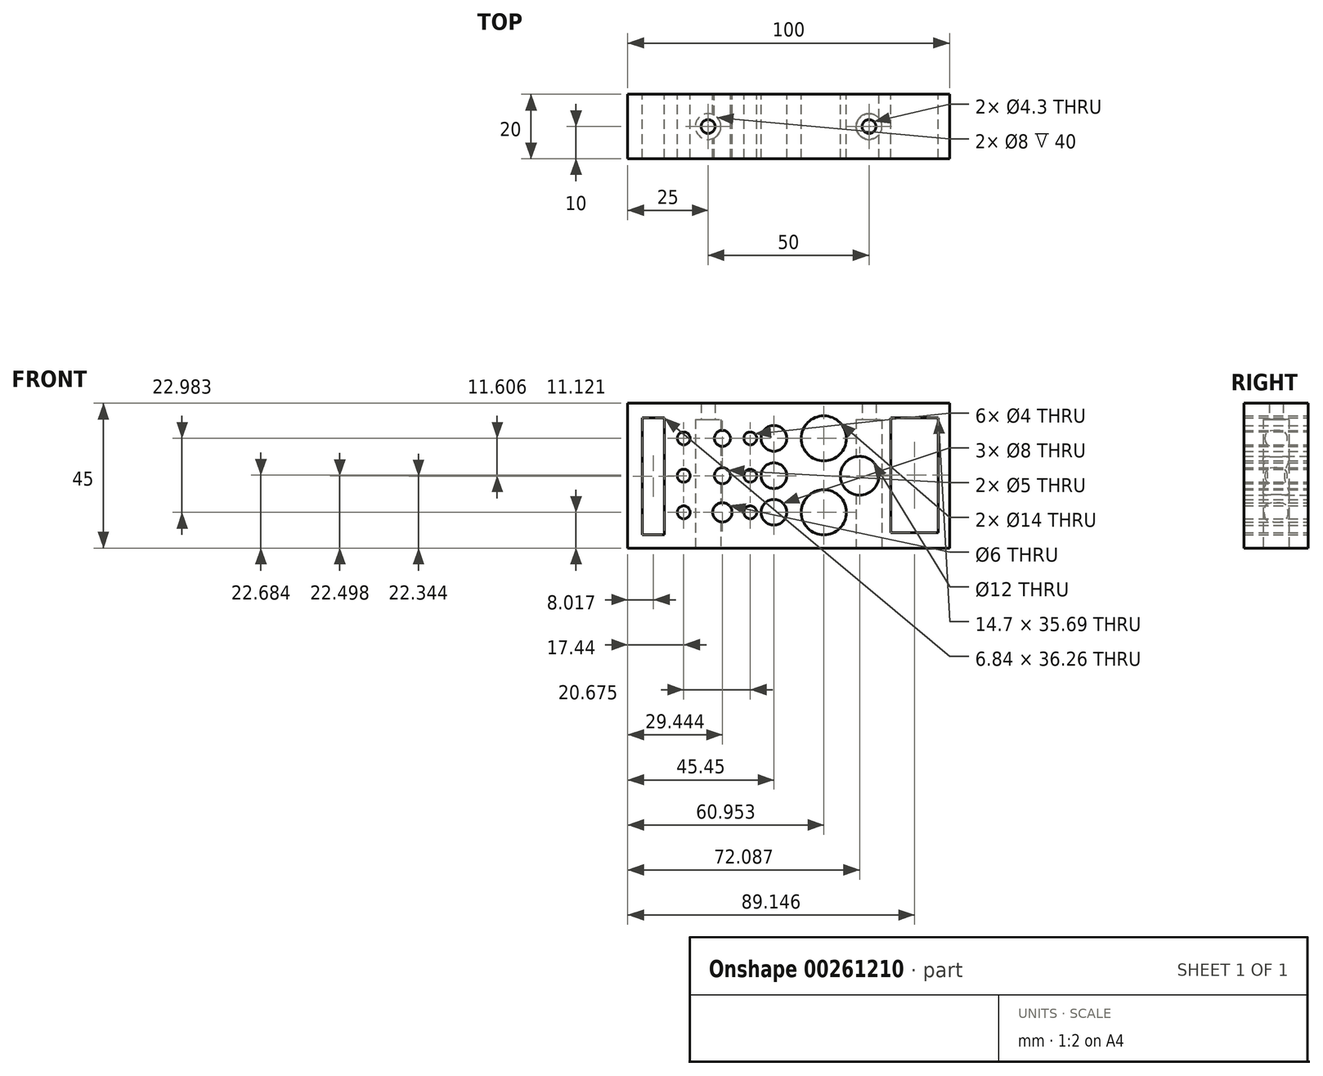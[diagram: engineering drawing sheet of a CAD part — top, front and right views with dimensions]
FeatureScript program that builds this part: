
annotation { "Feature Type Name" : "Feature", "Feature Type Description" : "" }
export const myFeature = defineFeature(function(context is Context, id is Id, definition is map)
    precondition{}
    {
        {
            var Q0;
            Q0=qCreatedBy(makeId("Front.planeOp"),FACE);
            var sketch = newSketch(context, id + "F0", { "sketchPlane" : qUnion([Q0])});
            skLineSegment(sketch, "E0.bottom", {"start": v(-53.57, 64.8) * mm, "end": v(46.43, 64.8) * mm});
            skLineSegment(sketch, "E0.top", {"start": v(-53.57, 19.8) * mm, "end": v(46.43, 19.8) * mm});
            skLineSegment(sketch, "E0.left", {"start": v(-53.57, 64.8) * mm, "end": v(-53.57, 19.8) * mm});
            skLineSegment(sketch, "E0.right", {"start": v(46.43, 64.8) * mm, "end": v(46.43, 19.8) * mm});
            skLineSegment(sketch, "E1.bottom", {"start": v(-48.97, 60.28) * mm, "end": v(-42.13, 60.28) * mm});
            skLineSegment(sketch, "E1.top", {"start": v(-48.97, 24.03) * mm, "end": v(-42.13, 24.03) * mm});
            skLineSegment(sketch, "E1.left", {"start": v(-48.97, 60.28) * mm, "end": v(-48.97, 24.03) * mm});
            skLineSegment(sketch, "E1.right", {"start": v(-42.13, 60.28) * mm, "end": v(-42.13, 24.03) * mm});
            skLineSegment(sketch, "E2", {"start": v(-53.57, 42.3) * mm, "end": v(46.43, 42.3) * mm, "construction": true});
            skLineSegment(sketch, "E3", {"start": v(0, 64.8) * mm, "end": v(0, 19.8) * mm, "construction": true});
            skLineSegment(sketch, "E4", {"start": v(-36.13, 64.8) * mm, "end": v(-36.13, 19.8) * mm, "construction": true});
            skLineSegment(sketch, "E5", {"start": v(-30.32, 64.8) * mm, "end": v(-30.32, 19.8) * mm, "construction": true});
            skLineSegment(sketch, "E6", {"start": v(-24.13, 64.8) * mm, "end": v(-24.13, 19.8) * mm, "construction": true});
            skLineSegment(sketch, "E7", {"start": v(-15.46, 64.8) * mm, "end": v(-15.46, 19.8) * mm, "construction": true});
            skLineSegment(sketch, "E8", {"start": v(-8.12, 64.8) * mm, "end": v(-8.12, 19.8) * mm, "construction": true});
            skLineSegment(sketch, "E9", {"start": v(7.38, 64.8) * mm, "end": v(7.38, 19.8) * mm, "construction": true});
            skLineSegment(sketch, "E10", {"start": v(18.52, 64.8) * mm, "end": v(18.52, 19.8) * mm, "construction": true});
            skLineSegment(sketch, "E11", {"start": v(28.22, 64.8) * mm, "end": v(28.22, 19.8) * mm, "construction": true});
            skLineSegment(sketch, "E12", {"start": v(-53.57, 30.93) * mm, "end": v(46.43, 30.93) * mm, "construction": true});
            skLineSegment(sketch, "E13", {"start": v(-53.57, 53.91) * mm, "end": v(46.43, 53.91) * mm, "construction": true});
            skCircle(sketch, "E14", {"center": v(-36.13, 42.3) * mm, "radius": 2 * mm});
            skCircle(sketch, "E15", {"center": v(-36.13, 53.91) * mm, "radius": 2 * mm});
            skCircle(sketch, "E16", {"center": v(-36.13, 30.93) * mm, "radius": 2 * mm});
            skCircle(sketch, "E17", {"center": v(-24.13, 53.91) * mm, "radius": 2.5 * mm});
            skCircle(sketch, "E18", {"center": v(-24.13, 42.3) * mm, "radius": 2.5 * mm});
            skCircle(sketch, "E19", {"center": v(-24.13, 30.93) * mm, "radius": 3 * mm});
            skCircle(sketch, "E20", {"center": v(-8.12, 53.91) * mm, "radius": 4 * mm});
            skCircle(sketch, "E21", {"center": v(-8.12, 42.3) * mm, "radius": 4 * mm});
            skCircle(sketch, "E22", {"center": v(-8.12, 30.93) * mm, "radius": 4 * mm});
            skCircle(sketch, "E23", {"center": v(7.38, 53.91) * mm, "radius": 7 * mm});
            skCircle(sketch, "E24", {"center": v(7.38, 30.93) * mm, "radius": 7 * mm});
            skCircle(sketch, "E25", {"center": v(18.52, 42.3) * mm, "radius": 6 * mm});
            skLineSegment(sketch, "E26.bottom", {"start": v(28.22, 60.34) * mm, "end": v(42.93, 60.34) * mm});
            skLineSegment(sketch, "E26.top", {"start": v(28.22, 24.65) * mm, "end": v(42.93, 24.65) * mm});
            skLineSegment(sketch, "E26.left", {"start": v(28.22, 60.34) * mm, "end": v(28.22, 24.65) * mm});
            skLineSegment(sketch, "E26.right", {"start": v(42.93, 60.34) * mm, "end": v(42.93, 24.65) * mm});
            skCircle(sketch, "E27", {"center": v(-15.46, 53.91) * mm, "radius": 2 * mm});
            skCircle(sketch, "E28", {"center": v(-15.46, 42.3) * mm, "radius": 2 * mm});
            skCircle(sketch, "E29", {"center": v(-15.46, 30.93) * mm, "radius": 2 * mm});
            skSolve(sketch);
        }
        {
            var Q0;
            Q0=qSketchRegion(id+"F0",true);
            extrude(context, id + "F1", {"entities" : qUnion([Q0]), "depth" : 20 * mm});
        }
        {
            var Q0;
            Q0=makeQuery(id+"F1.opExtrude","SWEPT_FACE",FACE,{"disambiguationData":[OSD([sQuery(id+"F0.wireOp",EDGE,"E0.top")])]});
            var sketch = newSketch(context, id + "F2", { "sketchPlane" : qUnion([Q0])});
            skLineSegment(sketch, "E30", {"start": v(-53.57, 10) * mm, "end": v(46.43, 10) * mm, "construction": true});
            skLineSegment(sketch, "E31", {"start": v(-53.57, 0) * mm, "end": v(-3.57, 20) * mm, "construction": true});
            skLineSegment(sketch, "E32", {"start": v(-3.57, 20) * mm, "end": v(46.43, 0) * mm, "construction": true});
            skCircle(sketch, "E33", {"center": v(-28.57, 10) * mm, "radius": 2.15 * mm});
            skCircle(sketch, "E34", {"center": v(21.43, 10) * mm, "radius": 2.15 * mm});
            skSolve(sketch);
        }
        {
            var Q0;
            Q0=makeQuery(id+"F2.imprint","IMPRINT",FACE,{"disambiguationData":[TD([[makeQuery(id+"F2.imprint","IMPRINT",EDGE,{"derivedFrom":sQuery(id+"F2.wireOp",EDGE,"E34")}),1.0]])]});
            var Q1;
            Q1=makeQuery(id+"F2.imprint","IMPRINT",FACE,{"disambiguationData":[TD([[makeQuery(id+"F2.imprint","IMPRINT",EDGE,{"derivedFrom":sQuery(id+"F2.wireOp",EDGE,"E33")}),1.0]])]});
            extrude(context, id + "F3", {"entities" : qUnion([Q0, Q1]), "operationType" : NewBodyOperationType.REMOVE, "oppositeDirection" : true, "depth" : 50 * mm});
        }
        {
            var Q0;
            Q0=makeQuery(id+"F1.opExtrude","SWEPT_FACE",FACE,{"disambiguationData":[OSD([sQuery(id+"F0.wireOp",EDGE,"E0.top")])]});
            var sketch = newSketch(context, id + "F4", { "sketchPlane" : qUnion([Q0])});
            skCircle(sketch, "E35", {"center": v(-28.57, 10) * mm, "radius": 4 * mm});
            skCircle(sketch, "E36", {"center": v(21.43, 10) * mm, "radius": 4 * mm});
            skSolve(sketch);
        }
        {
            var Q0;
            Q0=qSketchRegion(id+"F4",true);
            extrude(context, id + "F5", {"entities" : qUnion([Q0]), "operationType" : NewBodyOperationType.REMOVE, "oppositeDirection" : true, "depth" : 40 * mm});
        }
    });
